# Revit family: 1
name_source: partatom
category: Plumbing Fixtures
revit_build: Autodesk Revit 2018 (Build: 20190510_1515(x64)
units: mm (PartAtom-declared; Revit-internal decimal feet)

## family parameters
Cut with Voids When Loaded = No
Host = Face
OmniClass Number = 23.31.13.00
OmniClass Title = Sinks
Part Type = Normal
Room Calculation Point = No
Round Connector Dimension = Use Diameter
Shared = No

## types (2) — shared parameters
BIMobject category = Wash basins
Connector Description = Water outlet
Default Elevation = 1219 mm
Design country = Germany
Detail material = Duravit - Metal - 10 - Chrome
ETIM classification = EC011550 | Washbasin
Edition number = 1
IFC Classification = Sanitary Terminal
Installation instructions = https://duravit-public-assets.s3.eu-central-1.amazonaws.com
Manufacturer = Duravit
Manufacturer name = DURAVIT AG
Masterformat 2014 Code = 22 41 16.13
Masterformat 2014 Description = Residential Lavatories
Material main = Ceramics
Model = Vero Hand sink 250 mm - 070225
OmniClass Code = 23-31 13 00
OmniClass Description = Sinks
Outlet Diameter = 32  [stored 0.104987 ft]
Product Guid = 756d6083-8a69-48a1-aba2-046b03f50d7d
Product SKU = Vero-Hand-sink-250-mm-070225
Product certification = http://pro.duravit.com
Product data url = https://bimobject.com
Product family = Vero
Product group = Hand sink
Product name = Vero Hand sink 250 mm - 070225
Product url = http://pro.duravit.com
QR code = https://bimobject.com
Technical description = http://pro.duravit.com
UNSPSC Code = 30181504
URL = https://www.duravit.com
Uniclass 2015 Code = Pr_40_20_96
Uniclass 2015 Name = Wash basins, sinks and troughs
Uniformat II Code = D2010
Uniformat II Description = Plumbing Fixtures
Weight Net (Kg) = 8,9
Youtube clip = http://pro.duravit.com

## per-type parameters (varying)
| type | Description | Main material |
| 00 - White Alpin WonderGliss | Duravit Vero Hand sink 250 mm White High Gloss, WonderGliss - 07022500001 | Duravit - Ceramic - 00 - White Alpin WonderGliss |
| 00 - White Alpin | Duravit Vero Hand sink 250 mm White High Gloss - 0702250000 | Duravit - Ceramic - 00 - White Alpin |

note: [stored X ft] marks values corroborated as IEEE doubles in the binary element streams (Revit-internal decimal feet)

## geometry (parser evidence)
native form markers: Sweep x3
no freeform markers — native parametric forms only
